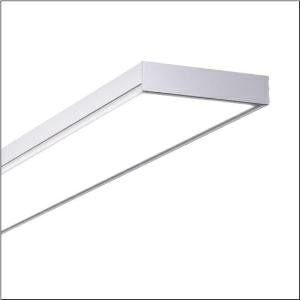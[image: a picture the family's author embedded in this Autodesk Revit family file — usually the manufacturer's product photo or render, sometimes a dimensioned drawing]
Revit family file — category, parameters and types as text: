
# Revit family: apollon_r__31_surface_51mp25wd2441e_f457
name_source: partatom
category: Lighting Fixtures
units: mm (PartAtom-declared; Revit-internal decimal feet)

## family parameters
Cut with Voids When Loaded = No
Host = Face
Light Source = No
Part Type = Normal
Room Calculation Point = No
Round Connector Dimension = Use Diameter
Shared = No

## types (1)
- Apollon® 31 Surface (1 x LED, 3800 lm, 28 W, 4000K)
    Apparent Load = 28 VA
    CIE Flux Codes = 61 87 97 97 100
    Color Rendering = 80
    Color Temperature = 4000K
    Default Elevation = 1800 mm
    Description = Apollon® 31 Surface, office luminaire, primary optical cover: micro prismatic cover, of PMMA, light emission: direct distribution, primary light characteristic: symmetric, installation type: surface-mounted, LED, rated luminous flux: 3.800lm, luminous efficacy: 134lm/W, light colour: 840, colour temperature: 4000K, control gear: ECG DALI, with terminal, 5-pole, mains connection: 220..240V, AC, 50/60Hz, rated input power: 28W, housing, of sheet steel, coil coated, metallic grey (RAL 9006), length: 1.245mm, width: 200mm, height: 44mm, protection rating (complete): IP20, insulation class (complete): insulation class II (safety insulation), certification: CE, impact resistance: IK02, permissible operating ambient temperature: -20..+40°C, standard: EN 60598-2-22, packaging unit: 1 piece
    Height = 44 mm
    Lamp = 1 x LED
    Lamp Light Flux = 3800 lm
    Lamp Power = 28 W
    Lamp count = 1
    Length = 1245 mm
    Luminous efficacy = 136 lm/W
    Manufacturer = Siteco
    ModVariant = No
    Model = 51MP25WD2441E
    Mounting Place = Ceiling
    Mounting Type = Surface mounted
    Number of Poles = 1
    OnlyDefault = Yes
    Power Factor = 1
    Product Name = Apollon® 31 Surface
    Product group = office luminaire | ceiling mounted
    ProductGroupID = 304
    Protection Class = Protection class II
    Protection Degree = IP 20
    RLX_Detail_Level = 1
    RLX_Emergency_Light_Flux = 0 lm
    RLX_Emergency_Type = 0
    RLX_Emergency_Type_DB = No
    RlxData = <blob elided: 24089 chars, md5=a62c031c>
    Socket = socket
    Standby Power = 0 W
    System Light Flux = 3800 lm
    System Power = 28 W
    Type Comments = Product without accessories
    Type Image = l_1007091.jpg
    URL = http://relux.com
    VarID = ---
    Voltage = 0 V
    Weight = 0.00 kg
    Width = 200 mm  [stored 0.656168 ft]

note: [stored X ft] marks values corroborated as IEEE doubles in the binary element streams (Revit-internal decimal feet)

## geometry (parser evidence)
native form markers: Blend x4, Sweep x9
no freeform markers — native parametric forms only
